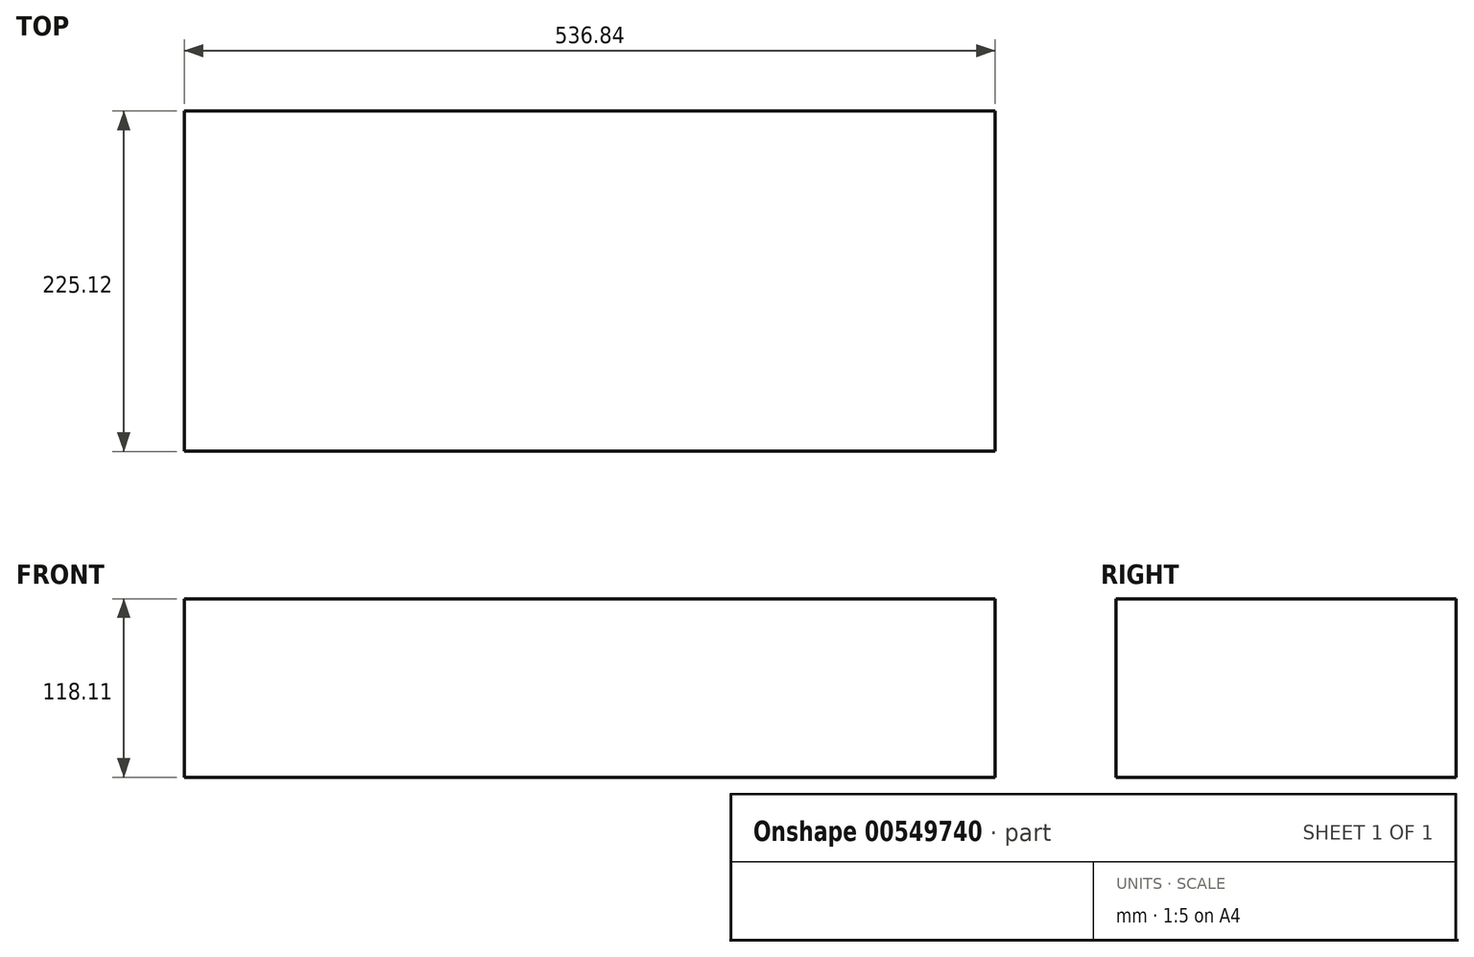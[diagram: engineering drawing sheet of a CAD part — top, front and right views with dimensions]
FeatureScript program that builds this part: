
annotation { "Feature Type Name" : "Feature", "Feature Type Description" : "" }
export const myFeature = defineFeature(function(context is Context, id is Id, definition is map)
    precondition{}
    {
        {
            var Q0;
            Q0=qCreatedBy(makeId("Top.planeOp"),FACE);
            var sketch = newSketch(context, id + "F0", { "sketchPlane" : qUnion([Q0])});
            skLineSegment(sketch, "E0.bottom", {"start": v(268.42, -112.56) * mm, "end": v(-268.42, -112.56) * mm});
            skLineSegment(sketch, "E0.top", {"start": v(268.42, 112.56) * mm, "end": v(-268.42, 112.56) * mm});
            skLineSegment(sketch, "E0.left", {"start": v(268.42, -112.56) * mm, "end": v(268.42, 112.56) * mm});
            skLineSegment(sketch, "E0.right", {"start": v(-268.42, -112.56) * mm, "end": v(-268.42, 112.56) * mm});
            skPoint(sketch, "E0.middle", {"position": v(0, 0) * mm});
            skSolve(sketch);
        }
        {
            var Q0;
            Q0=makeQuery(id+"F0.imprint","IMPRINT",FACE,{"disambiguationData":[TD([[makeQuery(id+"F0.imprint","IMPRINT",EDGE,{"derivedFrom":sQuery(id+"F0.wireOp",EDGE,"E0.bottom")}),-1.0]])]});
            extrude(context, id + "F1", {"entities" : qUnion([Q0]), "depth" : 118.1 * mm, "offsetDistance" : 25.4 * mm});
        }
    });
